# Revit family: P200635WX-134c_WUR50X24HZ
name_source: partatom
category: Specialty Equipment
units: mm (PartAtom-declared; Revit-internal decimal feet)

## family parameters
Always vertical = Yes
Cut with Voids When Loaded = No
Enable Cutting in Views = No
Maintain Annotation Orientation = No
Part Type = Normal
Room Calculation Point = No
Round Connector Dimension = Use Diameter
Shared = No
Work Plane-Based = No

## types (1)
- WUR50X24HZ
    Accent Material = ARCAT - Metal - Steel - Stainless
    Amps = 0 A
    Back Panel Material = ARCAT - Metal - Aluminum
    Body Material = ARCAT - Metal - Steel - Black
    Clearance Material = ARCAT - Clearance
    Default Elevation = 0"
    Depth = 25 5/8"
    Description = 24-inch Wide Undercounter Refrigerator - 5.1 cu. ft.
Réfrigérateur sous le comptoir, 24 po, 5.1 pi³
    Dimension Guide = http://access.whirlpool.com Guide&sku=WUR50X24HZ&language=EN
http://access.whirlpool.com Guide&sku=WUR50X24HZ&language=EN
    Door Material = ARCAT - Metal - Steel - Stainless
    Energy Guide = http://access.whirlpool.com Guide&sku=WUR50X24HZ&language=EN
http://access.whirlpool.com Guide&sku=WUR50X24HZ&language=EN
    Family Name = Undercounter Refrigerator
    Feature 1 = Single-Temperature Controlled Zone
Zone unique à température contrôlée
    Feature 2 = LED Interior Lighting
Éclairage intérieur à DEL
    Feature 3 = Reversible Stainless Steel Door
Porte réversible en acier inoxydable
    Handle Material = ARCAT - Metal - Steel - Grey
    Height = 35"
    Leg Material = ARCAT - Plastic - Black
    Manufacturer = Whirlpool
    Model = WUR50X24HZ
    Voltage = 0 V
    Width = 23 15/16"

## geometry (parser evidence)
native form markers: Sweep x5
no freeform markers — native parametric forms only
